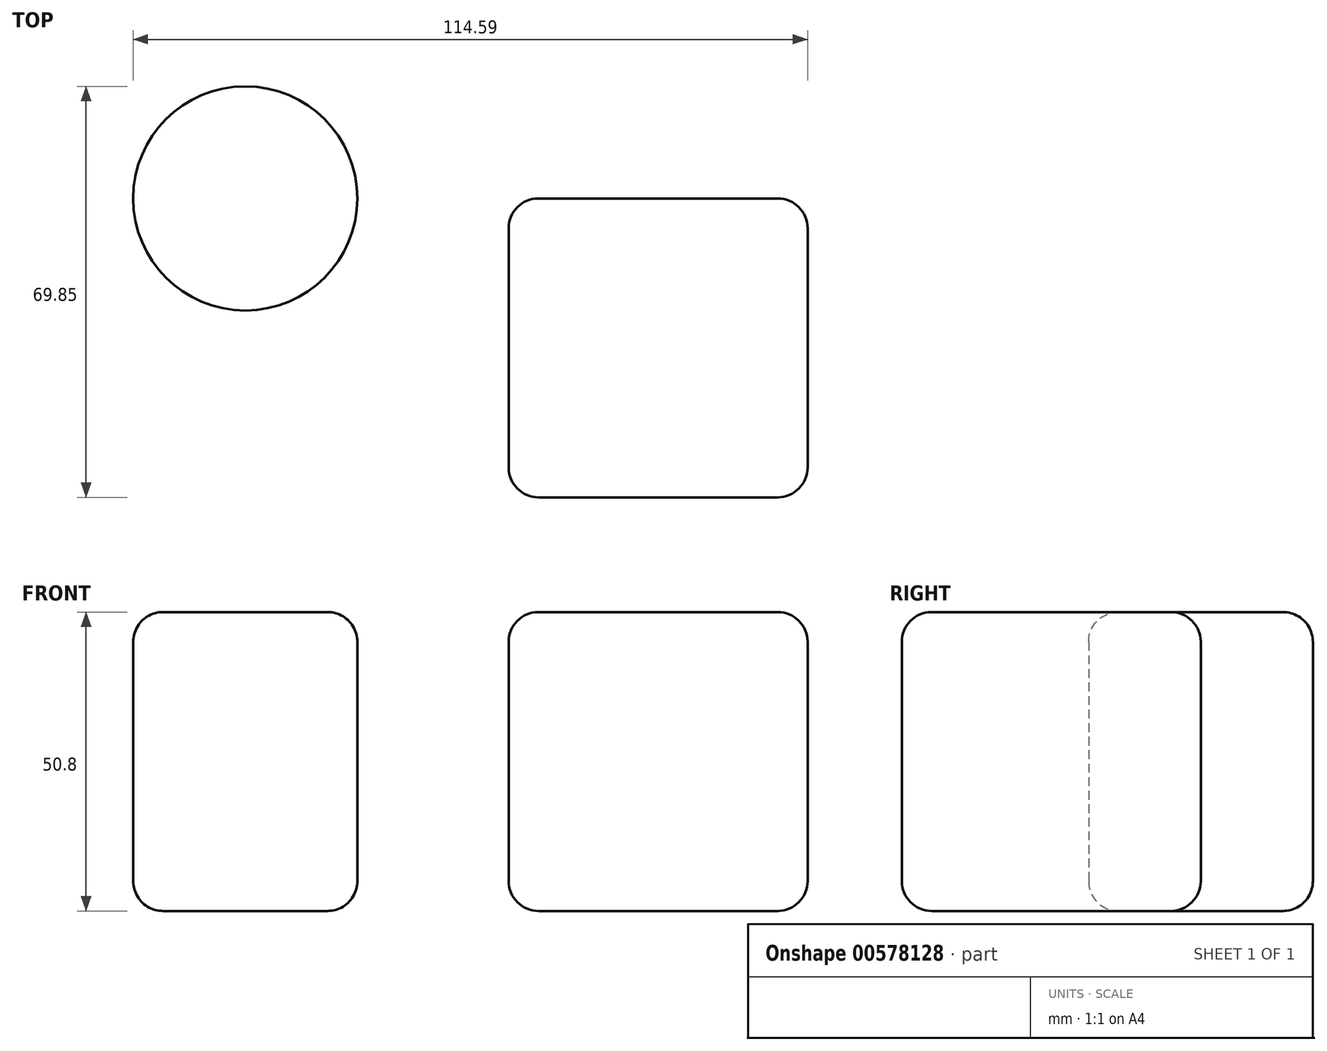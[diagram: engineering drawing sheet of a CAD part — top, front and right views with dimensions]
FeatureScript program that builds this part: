
annotation { "Feature Type Name" : "Feature", "Feature Type Description" : "" }
export const myFeature = defineFeature(function(context is Context, id is Id, definition is map)
    precondition{}
    {
        {
            var Q0;
            Q0=qCreatedBy(makeId("Top.planeOp"),FACE);
            var sketch = newSketch(context, id + "F0", { "sketchPlane" : qUnion([Q0])});
            skLineSegment(sketch, "E0.bottom", {"start": v(0, 0) * mm, "end": v(-50.8, 0) * mm});
            skLineSegment(sketch, "E0.top", {"start": v(0, -50.8) * mm, "end": v(-50.8, -50.8) * mm});
            skLineSegment(sketch, "E0.left", {"start": v(0, 0) * mm, "end": v(0, -50.8) * mm});
            skLineSegment(sketch, "E0.right", {"start": v(-50.8, 0) * mm, "end": v(-50.8, -50.8) * mm});
            skCircle(sketch, "E1", {"center": v(-95.54, 0) * mm, "radius": 19.05 * mm});
            skSolve(sketch);
        }
        {
            var Q0;
            Q0 = qSketchRegion(id + "F0", true);
            extrude(context, id + "F1", {"entities" : qUnion([Q0]), "depth" : 50.8 * mm, "offsetDistance" : 25.4 * mm});
        }
        {
            var Q0;
            Q0=makeQuery(id+"F1.opExtrude","CAP_FACE",FACE,{"disambiguationData":[OSD([sQuery(id+"F0.wireOp",EDGE,"E1")])],"isStart":false});
            var Q1;
            Q1=makeQuery(id+"F1.opExtrude","SWEPT_FACE",FACE,{"disambiguationData":[OSD([sQuery(id+"F0.wireOp",EDGE,"E0.right")])]});
            var Q2;
            Q2=makeQuery(id+"F1.opExtrude","CAP_EDGE",EDGE,{"disambiguationData":[OSD([sQuery(id+"F0.wireOp",EDGE,"E0.right")])],"isStart":false});
            var Q3;
            Q3=makeQuery(id+"F1.opExtrude","CAP_FACE",FACE,{"disambiguationData":[OSD([sQuery(id+"F0.wireOp",EDGE,"E0.bottom"),sQuery(id+"F0.wireOp",EDGE,"E0.top"),sQuery(id+"F0.wireOp",EDGE,"E0.left"),sQuery(id+"F0.wireOp",EDGE,"E0.right")])],"isStart":false});
            var Q4;
            Q4=makeQuery(id+"F1.opExtrude","SWEPT_EDGE",EDGE,{"disambiguationData":[OSD([sQuery(id+"F0.wireOp",EDGE,"E0.top"),sQuery(id+"F0.wireOp",EDGE,"E0.left")])]});
            var Q5;
            Q5=makeQuery(id+"F1.opExtrude","SWEPT_EDGE",EDGE,{"disambiguationData":[OSD([sQuery(id+"F0.wireOp",EDGE,"E0.bottom"),sQuery(id+"F0.wireOp",EDGE,"E0.left")])]});
            var Q6;
            Q6=makeQuery(id+"F1.opExtrude","SWEPT_FACE",FACE,{"disambiguationData":[OSD([sQuery(id+"F0.wireOp",EDGE,"E0.left")])]});
            var Q7;
            Q7=makeQuery(id+"F1.opExtrude","CAP_EDGE",EDGE,{"disambiguationData":[OSD([sQuery(id+"F0.wireOp",EDGE,"E0.top")])],"isStart":true});
            var Q8;
            Q8=makeQuery(id+"F1.opExtrude","CAP_EDGE",EDGE,{"disambiguationData":[OSD([sQuery(id+"F0.wireOp",EDGE,"E0.bottom")])],"isStart":true});
            var Q9;
            Q9=makeQuery(id+"F1.opExtrude","CAP_EDGE",EDGE,{"disambiguationData":[OSD([sQuery(id+"F0.wireOp",EDGE,"E1")])],"isStart":true});
            fillet(context, id + "F2", {"entities" : qUnion([Q0, Q1, Q2, Q3, Q4, Q5, Q6, Q7, Q8, Q9]), "radius" : 5.08 * mm, "tangentPropagation" : true, "allowEdgeOverflow" : false});
        }
    });
